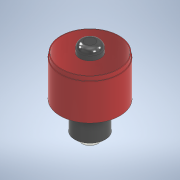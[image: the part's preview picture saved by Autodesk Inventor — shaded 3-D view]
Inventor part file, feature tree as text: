
AUTODESK INVENTOR PART (.ipt)
format: ipt  version: 2020 (Build 240168000, 168)  size: 147,456 bytes
history: native  units: in
note: dims shown in document units (in); Inventor stores cm internally (conversion verified against a paired STEP export)
features: extrude x5, sketch x5, fillet x1, chamfer x1
ambient origin geometry x8: Origin, YZ Plane, XZ Plane, XY Plane, X Axis, Y Axis, Z Axis, Center Point
bodies: Solid1 (feature_tree)
feature tree (12):
  extrude  "Extrusion1"  Depth=1.0236in TaperAngle=0.0deg
  extrude  "Extrusion2"  Depth=0.1181in TaperAngle=0.0deg
  extrude  "Extrusion3"  Depth=1.1417in TaperAngle=0.0deg
  extrude  "Extrusion4"  Depth=0.2756in TaperAngle=0.0deg
  fillet  "Fillet1"  Radius=0.1575in
  extrude  "Extrusion5"  Depth=0.9843in TaperAngle=0.0deg
  chamfer  "Chamfer1"  Distance=0.1969in Angle=45.0deg
  sketch  "Sketch1"  dims[d0=1.6929in d1=1.0236in d2=0.0in]
  sketch  "Sketch2"  dims[d3=1.6535in d4=0.1181in d5=0.0in]
  sketch  "Sketch3"  dims[d6=1.6142in d7=1.1417in d8=0.0in]
  sketch  "Sketch4"  dims[d9=0.5906in d10=0.2756in d11=0.0in d12=0.1575in]
  sketch  "Sketch5"  dims[d13=0.8661in d14=0.9843in d15=0.0in d16=0.1969in d17=0.0787in d18=45.0deg]
